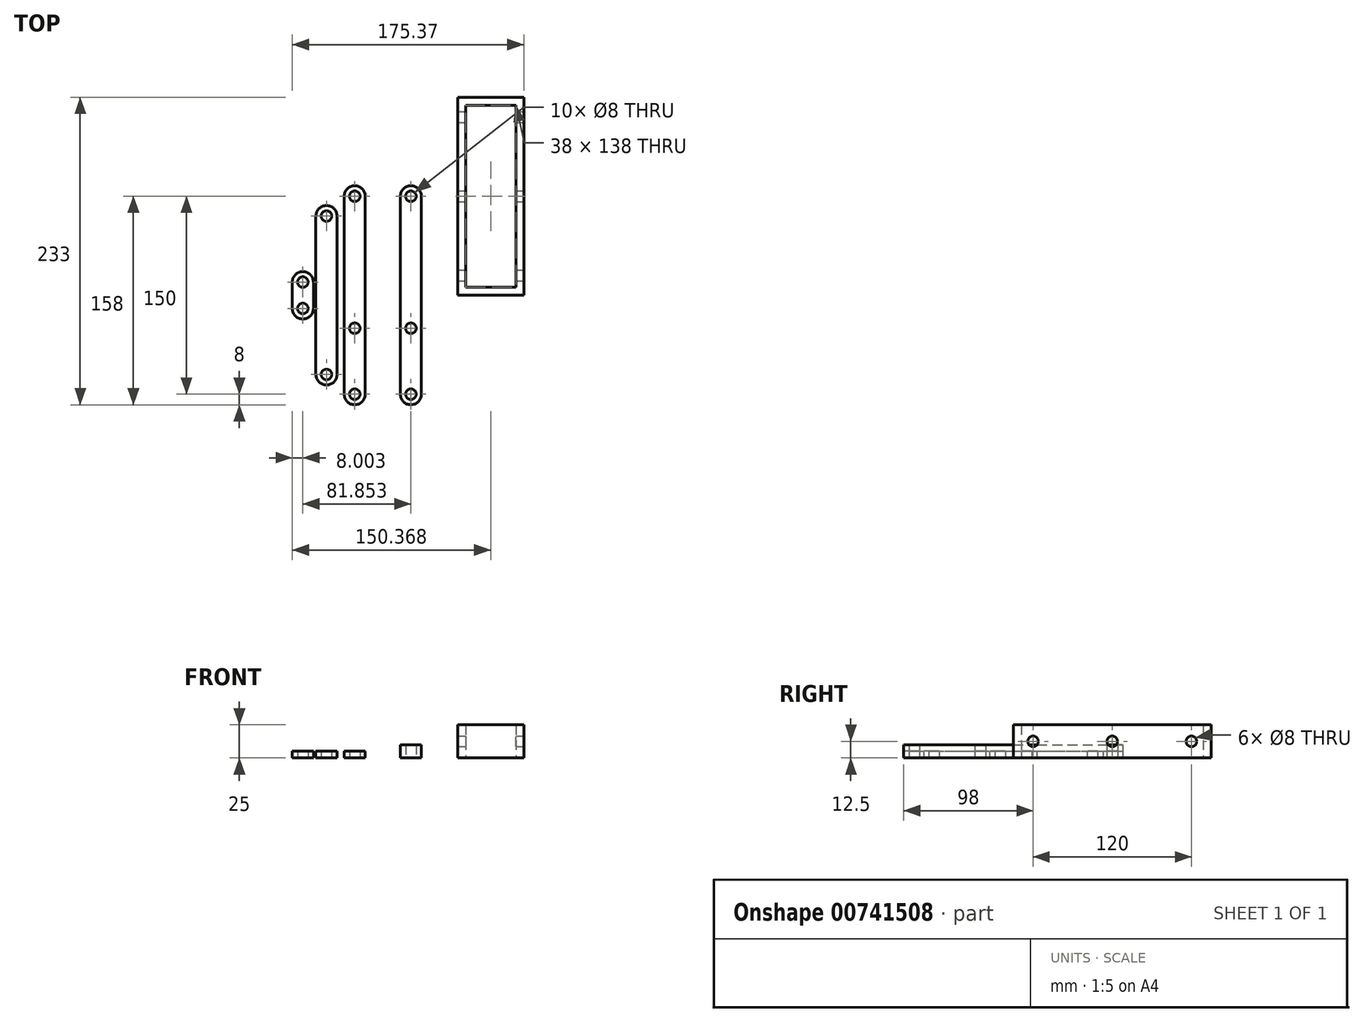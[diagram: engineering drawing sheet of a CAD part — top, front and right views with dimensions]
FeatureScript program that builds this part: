
annotation { "Feature Type Name" : "Feature", "Feature Type Description" : "" }
export const myFeature = defineFeature(function(context is Context, id is Id, definition is map)
    precondition{}
    {
        {
            var Q0;
            Q0=qCreatedBy(makeId("Top.planeOp"),FACE);
            var sketch = newSketch(context, id + "F0", { "sketchPlane" : qUnion([Q0])});
            skLineSegment(sketch, "E0", {"start": v(53.93, 0) * mm, "end": v(53.93, 150) * mm});
            skLineSegment(sketch, "E1", {"start": v(53.93, 150) * mm, "end": v(103.93, 150) * mm});
            skLineSegment(sketch, "E2", {"start": v(103.93, 150) * mm, "end": v(103.93, 0) * mm});
            skLineSegment(sketch, "E3", {"start": v(59.93, 144) * mm, "end": v(97.93, 144) * mm});
            skLineSegment(sketch, "E4", {"start": v(97.93, 144) * mm, "end": v(97.93, 6) * mm});
            skLineSegment(sketch, "E5", {"start": v(97.93, 6) * mm, "end": v(59.93, 6) * mm});
            skLineSegment(sketch, "E6", {"start": v(59.93, 6) * mm, "end": v(59.93, 144) * mm});
            skLineSegment(sketch, "E7", {"start": v(103.93, 0) * mm, "end": v(53.93, 0) * mm});
            skSolve(sketch);
        }
        {
            var Q0;
            Q0 = qSketchRegion(id + "F0", true);
            extrude(context, id + "F1", {"entities" : qUnion([Q0]), "depth" : 25 * mm, "offsetDistance" : 25 * mm});
        }
        {
            var Q0;
            Q0=qCreatedBy(makeId("Top.planeOp"),FACE);
            var sketch = newSketch(context, id + "F2", { "sketchPlane" : qUnion([Q0])});
            skLineSegment(sketch, "E8", {"start": v(-16.13, 0) * mm, "end": v(-16.13, 75) * mm});
            skLineSegment(sketch, "E9", {"start": v(-32.13, 75) * mm, "end": v(-32.13, 0) * mm});
            skArc(sketch, "E10", {"start": v(-16.13, 75) * mm, "mid": v(-24.13, 83) * mm, "end": v(-32.13, 75) * mm});
            skCircle(sketch, "E11", {"center": v(-24.13, 75) * mm, "radius": 4 * mm});
            skLineSegment(sketch, "E12", {"start": v(-24.13, 90.66) * mm, "end": v(-24.13, -16.39) * mm, "construction": true});
            skLineSegment(sketch, "E13.MirrorCS", {"start": v(-16.13, 0) * mm, "end": v(-16.13, -75) * mm});
            skLineSegment(sketch, "E14.MirrorCS", {"start": v(-32.13, -75) * mm, "end": v(-32.13, 0) * mm});
            skArc(sketch, "E15.MirrorCS", {"start": v(-16.13, -75) * mm, "mid": v(-24.13, -83) * mm, "end": v(-32.13, -75) * mm});
            skCircle(sketch, "E16.MirrorC", {"center": v(-24.13, -75) * mm, "radius": 4 * mm});
            skCircle(sketch, "E17", {"center": v(-24.13, -25) * mm, "radius": 4 * mm});
            skSolve(sketch);
        }
        {
            var Q0;
            Q0=makeQuery(id+"F2.imprint","IMPRINT",FACE,{"disambiguationData":[TD([[makeQuery(id+"F2.imprint","IMPRINT",EDGE,{"derivedFrom":sQuery(id+"F2.wireOp",EDGE,"E8")}),1.0]])]});
            extrude(context, id + "F3", {"entities" : qUnion([Q0]), "depth" : 5 * mm, "offsetDistance" : 25 * mm});
        }
        {
            var Q0;
            Q0=qCreatedBy(makeId("Top.planeOp"),FACE);
            var sketch = newSketch(context, id + "F4", { "sketchPlane" : qUnion([Q0])});
            skLineSegment(sketch, "E18", {"start": v(-37.57, 0) * mm, "end": v(-37.57, 60) * mm});
            skLineSegment(sketch, "E19", {"start": v(-53.57, 60) * mm, "end": v(-53.57, 0) * mm});
            skArc(sketch, "E20", {"start": v(-37.57, 60) * mm, "mid": v(-45.57, 68) * mm, "end": v(-53.57, 60) * mm});
            skLineSegment(sketch, "E21", {"start": v(-45.57, 78.54) * mm, "end": v(-45.57, -25.33) * mm, "construction": true});
            skCircle(sketch, "E22", {"center": v(-45.57, 60) * mm, "radius": 4 * mm});
            skLineSegment(sketch, "E23.MirrorCS", {"start": v(-37.57, 0) * mm, "end": v(-37.57, -60) * mm});
            skLineSegment(sketch, "E24.MirrorCS", {"start": v(-53.57, -60) * mm, "end": v(-53.57, 0) * mm});
            skCircle(sketch, "E25.MirrorC", {"center": v(-45.57, -60) * mm, "radius": 4 * mm});
            skArc(sketch, "E26.MirrorCS", {"start": v(-37.57, -60) * mm, "mid": v(-45.57, -68) * mm, "end": v(-53.57, -60) * mm});
            skSolve(sketch);
        }
        {
            var Q0;
            Q0 = qSketchRegion(id + "F4", true);
            extrude(context, id + "F5", {"entities" : qUnion([Q0]), "depth" : 5 * mm, "offsetDistance" : 25 * mm});
        }
        {
            var Q0;
            Q0=makeQuery(id+"F1.opExtrude","SWEPT_FACE",FACE,{"disambiguationData":[OSD([sQuery(id+"F0.wireOp",EDGE,"E2")])]});
            var sketch = newSketch(context, id + "F6", { "sketchPlane" : qUnion([Q0])});
            skCircle(sketch, "E27", {"center": v(15, 12.5) * mm, "radius": 4 * mm});
            skPoint(sketch, "E27.centerSnap0", {"position": v(0, 12.5) * mm});
            skCircle(sketch, "E28", {"center": v(75, 12.5) * mm, "radius": 4 * mm});
            skPoint(sketch, "E28.centerSnap0", {"position": v(75, 25) * mm});
            skCircle(sketch, "E29", {"center": v(135, 12.5) * mm, "radius": 4 * mm});
            skSolve(sketch);
        }
        {
            var Q0;
            Q0=makeQuery(id+"F6.imprint","IMPRINT",FACE,{"disambiguationData":[TD([[makeQuery(id+"F6.imprint","IMPRINT",EDGE,{"derivedFrom":sQuery(id+"F6.wireOp",EDGE,"E27")}),1.0]])]});
            var Q1;
            Q1=makeQuery(id+"F6.imprint","IMPRINT",FACE,{"disambiguationData":[TD([[makeQuery(id+"F6.imprint","IMPRINT",EDGE,{"derivedFrom":sQuery(id+"F6.wireOp",EDGE,"E28")}),1.0]])]});
            var Q2;
            Q2=makeQuery(id+"F6.imprint","IMPRINT",FACE,{"disambiguationData":[TD([[makeQuery(id+"F6.imprint","IMPRINT",EDGE,{"derivedFrom":sQuery(id+"F6.wireOp",EDGE,"E29")}),1.0]])]});
            extrude(context, id + "F7", {"entities" : qUnion([Q0, Q1, Q2]), "operationType" : NewBodyOperationType.REMOVE, "oppositeDirection" : true, "depth" : 67.1 * mm, "offsetDistance" : 25 * mm});
        }
        {
            var Q0;
            Q0=qCreatedBy(makeId("Top.planeOp"),FACE);
            var sketch = newSketch(context, id + "F8", { "sketchPlane" : qUnion([Q0])});
            skLineSegment(sketch, "E30", {"start": v(-55.44, 0) * mm, "end": v(-55.44, 10) * mm});
            skLineSegment(sketch, "E31", {"start": v(-71.44, 10) * mm, "end": v(-71.44, 0) * mm});
            skArc(sketch, "E32", {"start": v(-55.44, 10) * mm, "mid": v(-63.44, 18) * mm, "end": v(-71.44, 10) * mm});
            skCircle(sketch, "E33", {"center": v(-63.44, 10) * mm, "radius": 4 * mm});
            skLineSegment(sketch, "E34.MirrorCS", {"start": v(-55.44, 0) * mm, "end": v(-55.44, -10) * mm});
            skArc(sketch, "E35.MirrorCS", {"start": v(-55.44, -10) * mm, "mid": v(-63.44, -18) * mm, "end": v(-71.44, -10) * mm});
            skCircle(sketch, "E36.MirrorC", {"center": v(-63.44, -10) * mm, "radius": 4 * mm});
            skLineSegment(sketch, "E37.MirrorCS", {"start": v(-71.44, -10) * mm, "end": v(-71.44, 0) * mm});
            skSolve(sketch);
        }
        {
            var Q0;
            Q0=makeQuery(id+"F8.imprint","IMPRINT",FACE,{"disambiguationData":[TD([[makeQuery(id+"F8.imprint","IMPRINT",EDGE,{"derivedFrom":sQuery(id+"F8.wireOp",EDGE,"E30")}),1.0]])]});
            extrude(context, id + "F9", {"entities" : qUnion([Q0]), "depth" : 5 * mm, "offsetDistance" : 25 * mm});
        }
        {
            var Q0;
            Q0=qCreatedBy(makeId("Top.planeOp"),FACE);
            var sketch = newSketch(context, id + "F10", { "sketchPlane" : qUnion([Q0])});
            skLineSegment(sketch, "E38", {"start": v(26.42, 0) * mm, "end": v(26.42, 75) * mm});
            skLineSegment(sketch, "E39", {"start": v(10.42, 75) * mm, "end": v(10.42, 0) * mm});
            skArc(sketch, "E40", {"start": v(26.42, 75) * mm, "mid": v(18.42, 83) * mm, "end": v(10.42, 75) * mm});
            skCircle(sketch, "E41", {"center": v(18.42, 75) * mm, "radius": 4 * mm});
            skLineSegment(sketch, "E42.MirrorCS", {"start": v(26.42, 0) * mm, "end": v(26.42, -75) * mm});
            skLineSegment(sketch, "E43.MirrorCS", {"start": v(10.42, -75) * mm, "end": v(10.42, 0) * mm});
            skCircle(sketch, "E44.MirrorC", {"center": v(18.42, -75) * mm, "radius": 4 * mm});
            skArc(sketch, "E45.MirrorCS", {"start": v(26.42, -75) * mm, "mid": v(18.42, -83) * mm, "end": v(10.42, -75) * mm});
            skCircle(sketch, "E46", {"center": v(18.42, -25) * mm, "radius": 4 * mm});
            skSolve(sketch);
        }
        {
            var Q0;
            Q0=makeQuery(id+"F10.imprint","IMPRINT",FACE,{"disambiguationData":[TD([[makeQuery(id+"F10.imprint","IMPRINT",EDGE,{"derivedFrom":sQuery(id+"F10.wireOp",EDGE,"E38")}),1.0]])]});
            extrude(context, id + "F11", {"entities" : qUnion([Q0]), "depth" : 10 * mm, "offsetDistance" : 25 * mm});
        }
    });
